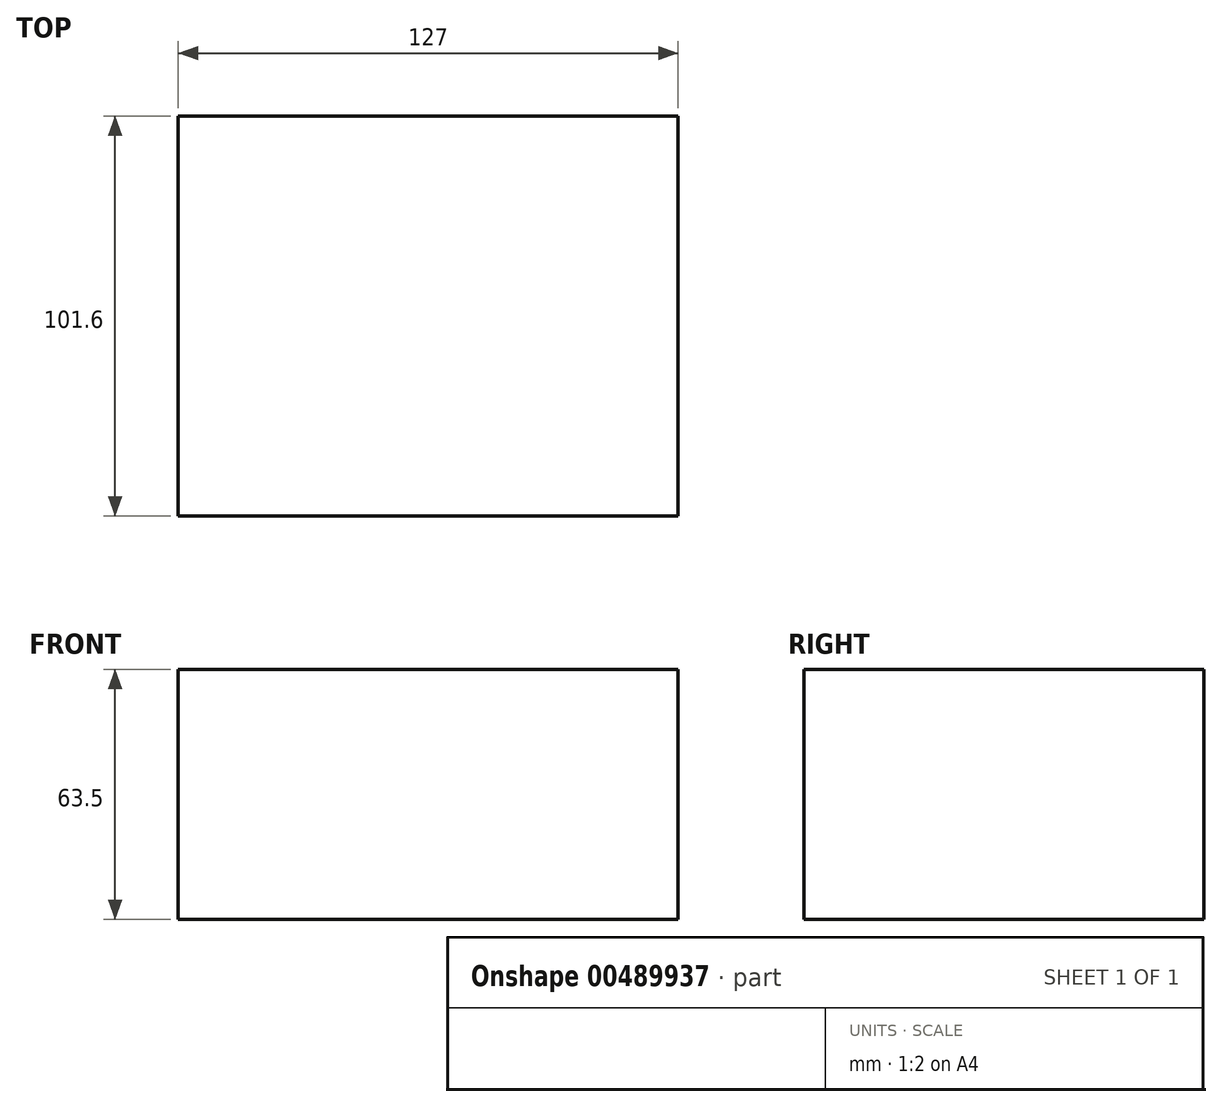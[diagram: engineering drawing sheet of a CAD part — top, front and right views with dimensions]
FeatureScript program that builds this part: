
annotation { "Feature Type Name" : "Feature", "Feature Type Description" : "" }
export const myFeature = defineFeature(function(context is Context, id is Id, definition is map)
    precondition{}
    {
        {
            var Q0;
            Q0=qCreatedBy(makeId("Front.planeOp"),FACE);
            var sketch = newSketch(context, id + "F0", { "sketchPlane" : qUnion([Q0])});
            skLineSegment(sketch, "E0.bottom", {"start": v(0, 63.5) * mm, "end": v(127, 63.5) * mm});
            skLineSegment(sketch, "E0.top", {"start": v(0, 0) * mm, "end": v(127, 0) * mm});
            skLineSegment(sketch, "E0.right", {"start": v(127, 63.5) * mm, "end": v(127, 0) * mm});
            skLineSegment(sketch, "E1", {"start": v(0, 63.5) * mm, "end": v(0, 0) * mm});
            skSolve(sketch);
        }
        {
            var Q0;
            Q0=makeQuery(id+"F0.imprint","IMPRINT",FACE,{"disambiguationData":[TD([[makeQuery(id+"F0.imprint","IMPRINT",EDGE,{"derivedFrom":sQuery(id+"F0.wireOp",EDGE,"E0.bottom")}),-1.0]])]});
            extrude(context, id + "F1", {"entities" : qUnion([Q0]), "depth" : 101.6 * mm});
        }
        {
            var Q0;
            Q0=makeQuery(id+"F1.opExtrude","CAP_FACE",FACE,{"disambiguationData":[OSD([sQuery(id+"F0.wireOp",EDGE,"E0.bottom"),sQuery(id+"F0.wireOp",EDGE,"E0.top"),sQuery(id+"F0.wireOp",EDGE,"E0.right"),sQuery(id+"F0.wireOp",EDGE,"E1")])],"isStart":false});
            var sketch = newSketch(context, id + "F2", { "sketchPlane" : qUnion([Q0])});
            skCircle(sketch, "E2", {"center": v(64, 31.5) * mm, "radius": 15.1 * mm});
            skSolve(sketch);
        }
        {
            var Q0;
            Q0=sQuery(id+"F2.wireOp",EDGE,"E2");
            var Q1;
            Q1=makeQuery(id+"F1.opExtrude","CAP_EDGE",EDGE,{"disambiguationData":[OSD([sQuery(id+"F0.wireOp",EDGE,"E0.right")])],"isStart":false});
            revolve(context, id + "F3", {"bodyType" : ToolBodyType.SURFACE, "surfaceEntities" : qUnion([Q0]), "axis" : qUnion([Q1]), "revolveType" : RevolveType.FULL});
        }
    });
